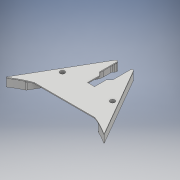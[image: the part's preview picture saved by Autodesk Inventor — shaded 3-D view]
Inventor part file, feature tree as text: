
AUTODESK INVENTOR PART (.ipt)
format: ipt  version: 2018 (Build 220112000, 112)  size: 271,872 bytes
history: native  units: mm
features: fillet x16, extrude x2, sketch x2, hole x1
ambient origin geometry x8: Origin, YZ Plane, XZ Plane, XY Plane, X Axis, Y Axis, Z Axis, Center Point
bodies: Solid1 (feature_tree)
feature tree (21):
  extrude  "Extrusion1"  Depth=2.0mm
  extrude  "Extrusion2"  Depth=0.5mm
  fillet  "Fillet1"  Radius=4.215mm
  fillet  "Fillet2"  Radius=126.01032mm
  fillet  "Fillet3"  Radius=175.894mm
  fillet  "Fillet4"  Radius=126.01032mm
  fillet  "Fillet5"  Radius=16.0mm
  fillet  "Fillet6"  Radius=4.215mm
  hole  "Hole1"  [1 undecoded]
  fillet  "Fillet13"  Radius=40.25mm
  fillet  "Fillet14"  Radius=5.0mm
  fillet  "Fillet15"  Radius=5.0mm
  fillet  "Fillet16"  Radius=2.0mm
  fillet  "Fillet17"  Radius=2.0mm
  fillet  "Fillet18"  Radius=5.0mm
  fillet  "Fillet19"  Radius=5.0mm
  fillet  "Fillet20"  Radius=376.0mm
  fillet  "Fillet21"  Radius=21.750293mm
  fillet  "Fillet22"  Radius=175.894mm
  sketch  "Sketch1"  dims[d31=2.0mm d32=0.0mm d39=175.894279mm]
  sketch  "Sketch3"  dims[d40=4.214555mm d41=40.25mm d45=4.215mm d66=126.01032mm d68=175.894mm d69=126.01032mm d71=16.0mm d72=0.0mm d73=4.215mm d74=4.215mm d75=40.25mm d76=5.0mm d77=5.0mm d78=2.0mm d79=2.0mm d86=5.0mm d87=5.0mm d88=376.0mm d89=21.750293mm d90=175.894mm d91=120.0deg d92=10.0mm d93=87.947mm d94=90.0deg d95=10.0mm d96=87.947mm d97=175.983619mm d98=5.0mm d99=6.0mm d100=10.0mm d101=13.0mm d102=90.0deg d103=18.0mm d104=20.594885mm d121=5.0mm d122=20.0mm d123=20.0mm d124=5.0mm d125=5.0mm d126=5.0mm d127=5.0mm d128=1.0mm d129=1.0mm d130=0.5mm d131=0.5mm]
note: 1 required parameter value undecoded (feature->parameter linkage not recoverable at this tier; creation-order binding heuristic only, values carry confidence <= 0.55)
